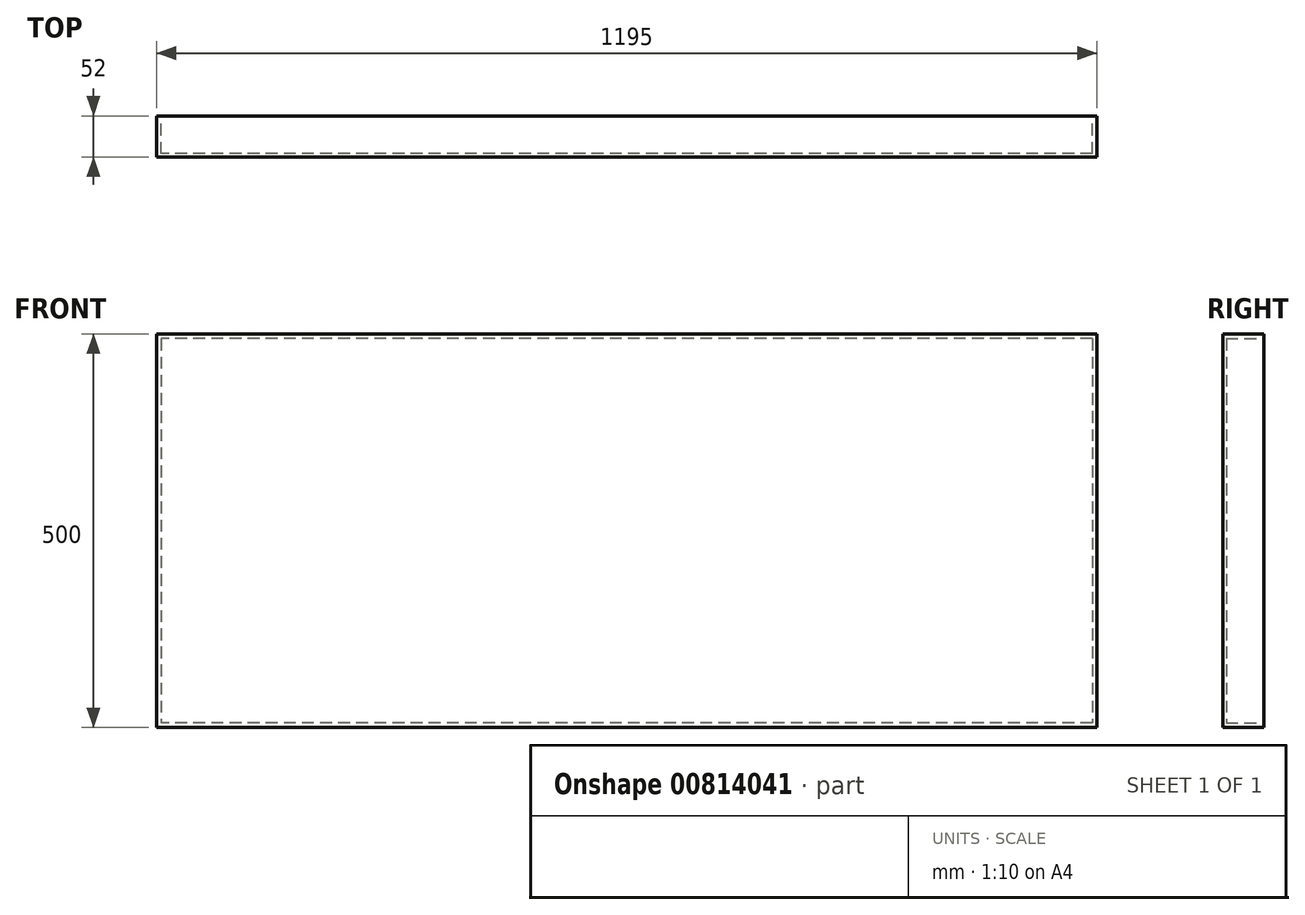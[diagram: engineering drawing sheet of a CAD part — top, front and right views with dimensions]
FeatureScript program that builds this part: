
annotation { "Feature Type Name" : "Feature", "Feature Type Description" : "" }
export const myFeature = defineFeature(function(context is Context, id is Id, definition is map)
    precondition{}
    {
        {
            var Q0;
            Q0=qCreatedBy(makeId("Front.planeOp"),FACE);
            var sketch = newSketch(context, id + "F0", { "sketchPlane" : qUnion([Q0])});
            skLineSegment(sketch, "E0.bottom", {"start": v(-597.5, 250) * mm, "end": v(597.5, 250) * mm});
            skLineSegment(sketch, "E0.top", {"start": v(-597.5, -250) * mm, "end": v(597.5, -250) * mm});
            skLineSegment(sketch, "E0.left", {"start": v(-597.5, 250) * mm, "end": v(-597.5, -250) * mm});
            skLineSegment(sketch, "E0.right", {"start": v(597.5, 250) * mm, "end": v(597.5, -250) * mm});
            skPoint(sketch, "E0.middle", {"position": v(0, 0) * mm});
            skSolve(sketch);
        }
        {
            var Q0;
            Q0 = qSketchRegion(id + "F0", true);
            extrude(context, id + "F1", {"entities" : qUnion([Q0]), "depth" : 52 * mm, "offsetDistance" : 25 * mm});
        }
        {
            var Q0;
            Q0=makeQuery(id+"F1.opExtrude","CAP_FACE",FACE,{"disambiguationData":[OSD([sQuery(id+"F0.wireOp",EDGE,"E0.bottom"),sQuery(id+"F0.wireOp",EDGE,"E0.top"),sQuery(id+"F0.wireOp",EDGE,"E0.left"),sQuery(id+"F0.wireOp",EDGE,"E0.right")])],"isStart":true});
            var sketch = newSketch(context, id + "F2", { "sketchPlane" : qUnion([Q0])});
            skLineSegment(sketch, "E1.bottom", {"start": v(-591.5, 244) * mm, "end": v(591.5, 244) * mm});
            skLineSegment(sketch, "E1.top", {"start": v(-591.5, -244) * mm, "end": v(591.5, -244) * mm});
            skLineSegment(sketch, "E1.left", {"start": v(-591.5, 244) * mm, "end": v(-591.5, -244) * mm});
            skLineSegment(sketch, "E1.right", {"start": v(591.5, 244) * mm, "end": v(591.5, -244) * mm});
            skPoint(sketch, "E1.middle", {"position": v(0, 0) * mm});
            skSolve(sketch);
        }
        {
            var Q0;
            Q0 = qSketchRegion(id + "F2", true);
            extrude(context, id + "F3", {"entities" : qUnion([Q0]), "operationType" : NewBodyOperationType.REMOVE, "oppositeDirection" : true, "depth" : 48 * mm, "offsetDistance" : 25 * mm});
        }
    });
